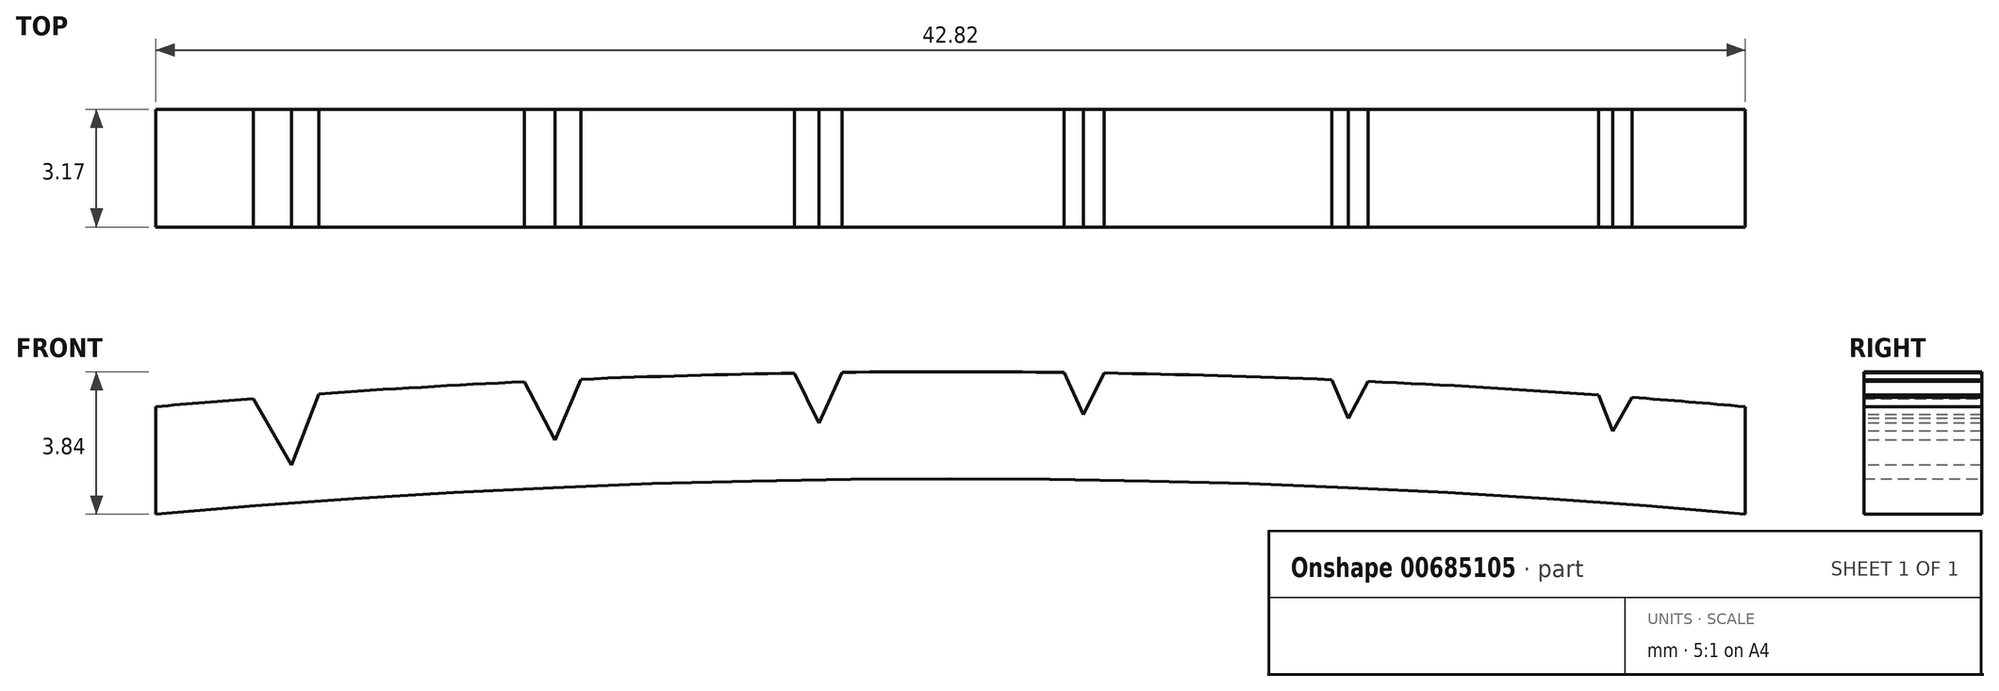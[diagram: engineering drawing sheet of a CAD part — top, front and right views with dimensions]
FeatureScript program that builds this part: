
annotation { "Feature Type Name" : "Feature", "Feature Type Description" : "" }
export const myFeature = defineFeature(function(context is Context, id is Id, definition is map)
    precondition{}
    {
        {
            var Q0;
            Q0=qCreatedBy(makeId("Top.planeOp"),FACE);
            var sketch = newSketch(context, id + "F0", { "sketchPlane" : qUnion([Q0])});
            skLineSegment(sketch, "E0.bottom", {"start": v(-21.41, 1.59) * mm, "end": v(21.41, 1.59) * mm});
            skLineSegment(sketch, "E0.top", {"start": v(-21.41, -1.59) * mm, "end": v(21.41, -1.59) * mm});
            skLineSegment(sketch, "E0.left", {"start": v(-21.41, 1.59) * mm, "end": v(-21.41, -1.59) * mm});
            skLineSegment(sketch, "E0.right", {"start": v(21.41, 1.59) * mm, "end": v(21.41, -1.59) * mm});
            skPoint(sketch, "E0.middle", {"position": v(0, 0) * mm});
            skLineSegment(sketch, "E1", {"start": v(-3.57, 1.59) * mm, "end": v(-3.57, -56.89) * mm, "construction": true});
            skLineSegment(sketch, "E2", {"start": v(3.57, 1.59) * mm, "end": v(3.57, -28.96) * mm, "construction": true});
            skLineSegment(sketch, "E3", {"start": v(0, 0) * mm, "end": v(0, -5.88) * mm, "construction": true});
            skPoint(sketch, "E3.endSnap0", {"position": v(0, -1.59) * mm});
            skLineSegment(sketch, "E4.1.0.0", {"start": v(10.7, 1.59) * mm, "end": v(10.7, -28.96) * mm, "construction": true});
            skLineSegment(sketch, "E4.2.0.0", {"start": v(17.84, 1.59) * mm, "end": v(17.84, -28.96) * mm, "construction": true});
            skLineSegment(sketch, "E4.direction1", {"start": v(3.57, -28.96) * mm, "end": v(10.7, -28.96) * mm, "construction": true});
            skLineSegment(sketch, "E5.1.0.0", {"start": v(-10.7, 1.59) * mm, "end": v(-10.7, -56.89) * mm, "construction": true});
            skLineSegment(sketch, "E5.2.0.0", {"start": v(-17.84, 1.59) * mm, "end": v(-17.84, -56.89) * mm, "construction": true});
            skLineSegment(sketch, "E5.direction1", {"start": v(-3.57, -56.89) * mm, "end": v(-10.7, -56.89) * mm, "construction": true});
            skSolve(sketch);
        }
        {
            var Q0;
            Q0=qCreatedBy(makeId("Front.planeOp"),FACE);
            var sketch = newSketch(context, id + "F1", { "sketchPlane" : qUnion([Q0])});
            skArc(sketch, "E6", {"start": v(21.41, -0.94) * mm, "mid": v(0, 0) * mm, "end": v(-21.41, -0.94) * mm});
            skLineSegment(sketch, "E7", {"start": v(21.41, -0.94) * mm, "end": v(21.41, -3.84) * mm});
            skLineSegment(sketch, "E8", {"start": v(-21.41, -0.94) * mm, "end": v(-21.41, -3.84) * mm});
            skArc(sketch, "E9", {"start": v(21.41, -3.84) * mm, "mid": v(0, -2.89) * mm, "end": v(-21.41, -3.84) * mm});
            skSolve(sketch);
        }
        {
            var Q0;
            Q0=qSketchRegion(id+"F1",true);
            extrude(context, id + "F2", {"entities" : qUnion([Q0]), "depth" : 3.17 * mm});
        }
        {
            var Q0;
            Q0=makeQuery(id+"F2.opExtrude","CAP_FACE",FACE,{"disambiguationData":[OSD([sQuery(id+"F1.wireOp",EDGE,"E6"),sQuery(id+"F1.wireOp",EDGE,"E7"),sQuery(id+"F1.wireOp",EDGE,"E8"),sQuery(id+"F1.wireOp",EDGE,"E9")])],"isStart":false});
            var sketch = newSketch(context, id + "F3", { "sketchPlane" : qUnion([Q0])});
            skLineSegment(sketch, "E10", {"start": v(-18.97, -0.38) * mm, "end": v(-17.76, -2.52) * mm});
            skLineSegment(sketch, "E11", {"start": v(-17.76, -2.52) * mm, "end": v(-16.88, -0.23) * mm});
            skPoint(sketch, "E12", {"position": v(-17.76, -2.52) * mm});
            skLineSegment(sketch, "E13", {"start": v(-18.97, -0.38) * mm, "end": v(-16.88, -0.23) * mm});
            skCircle(sketch, "E14", {"center": v(-17.84, -1.46) * mm, "radius": 0.46 * mm});
            skPoint(sketch, "E14.first.point", {"position": v(-18.24, -1.68) * mm});
            skPoint(sketch, "E14.second.point", {"position": v(-17.42, -1.62) * mm});
            skPoint(sketch, "E14.third.point", {"position": v(-17.84, -1) * mm});
            skLineSegment(sketch, "E15", {"start": v(-17.76, -2.52) * mm, "end": v(-17.69, -3.53) * mm, "construction": true});
            skLineSegment(sketch, "E16.1.0", {"start": v(-10.65, -1.85) * mm, "end": v(-9.7, 0.41) * mm});
            skLineSegment(sketch, "E16.1.1", {"start": v(-11.8, 0.32) * mm, "end": v(-10.65, -1.85) * mm});
            skLineSegment(sketch, "E16.1.3", {"start": v(-11.8, 0.32) * mm, "end": v(-9.7, 0.41) * mm});
            skLineSegment(sketch, "E16.2.0", {"start": v(-3.55, -1.39) * mm, "end": v(-2.53, 0.85) * mm});
            skLineSegment(sketch, "E16.2.1", {"start": v(-4.63, 0.82) * mm, "end": v(-3.55, -1.39) * mm});
            skLineSegment(sketch, "E16.2.3", {"start": v(-4.63, 0.82) * mm, "end": v(-2.53, 0.85) * mm});
            skPoint(sketch, "E16.center", {"position": v(0, -243.83) * mm});
            skLineSegment(sketch, "E16.anchor1", {"start": v(0, -243.83) * mm, "end": v(-17.76, -2.52) * mm, "construction": true});
            skLineSegment(sketch, "E17", {"start": v(0, -2.53) * mm, "end": v(0, -243.83) * mm, "construction": true});
            skLineSegment(sketch, "E18.1.3.0", {"start": v(3.58, -1.16) * mm, "end": v(4.66, 1.05) * mm});
            skLineSegment(sketch, "E18.3.3.0", {"start": v(2.56, 1.08) * mm, "end": v(3.58, -1.16) * mm});
            skLineSegment(sketch, "E18.8.3.0", {"start": v(2.56, 1.08) * mm, "end": v(4.66, 1.05) * mm});
            skLineSegment(sketch, "E18.1.4.0", {"start": v(10.7, -1.27) * mm, "end": v(11.86, 0.9) * mm});
            skLineSegment(sketch, "E18.3.4.0", {"start": v(9.76, 1) * mm, "end": v(10.7, -1.27) * mm});
            skLineSegment(sketch, "E18.8.4.0", {"start": v(9.76, 1) * mm, "end": v(11.86, 0.9) * mm});
            skLineSegment(sketch, "E18.1.5.0", {"start": v(17.83, -1.61) * mm, "end": v(19.05, 0.53) * mm});
            skLineSegment(sketch, "E18.3.5.0", {"start": v(16.95, 0.68) * mm, "end": v(17.83, -1.61) * mm});
            skLineSegment(sketch, "E18.8.5.0", {"start": v(16.95, 0.68) * mm, "end": v(19.05, 0.53) * mm});
            skLineSegment(sketch, "E19", {"start": v(-10.7, -0.68) * mm, "end": v(0, -243.83) * mm, "construction": true});
            skLineSegment(sketch, "E20", {"start": v(-3.57, -0.47) * mm, "end": v(0, -243.83) * mm, "construction": true});
            skLineSegment(sketch, "E21", {"start": v(3.59, -0.47) * mm, "end": v(0, -243.83) * mm, "construction": true});
            skLineSegment(sketch, "E22", {"start": v(10.74, -0.68) * mm, "end": v(0, -243.83) * mm, "construction": true});
            skLineSegment(sketch, "E23", {"start": v(17.87, -1.1) * mm, "end": v(0, -243.83) * mm, "construction": true});
            skSolve(sketch);
        }
        {
            var Q0;
            Q0=qSketchRegion(id+"F3",true);
            extrude(context, id + "F4", {"entities" : qUnion([Q0]), "operationType" : NewBodyOperationType.REMOVE, "endBound" : BoundingType.THROUGH_ALL, "oppositeDirection" : true, "depth" : 25.4 * mm});
        }
    });
